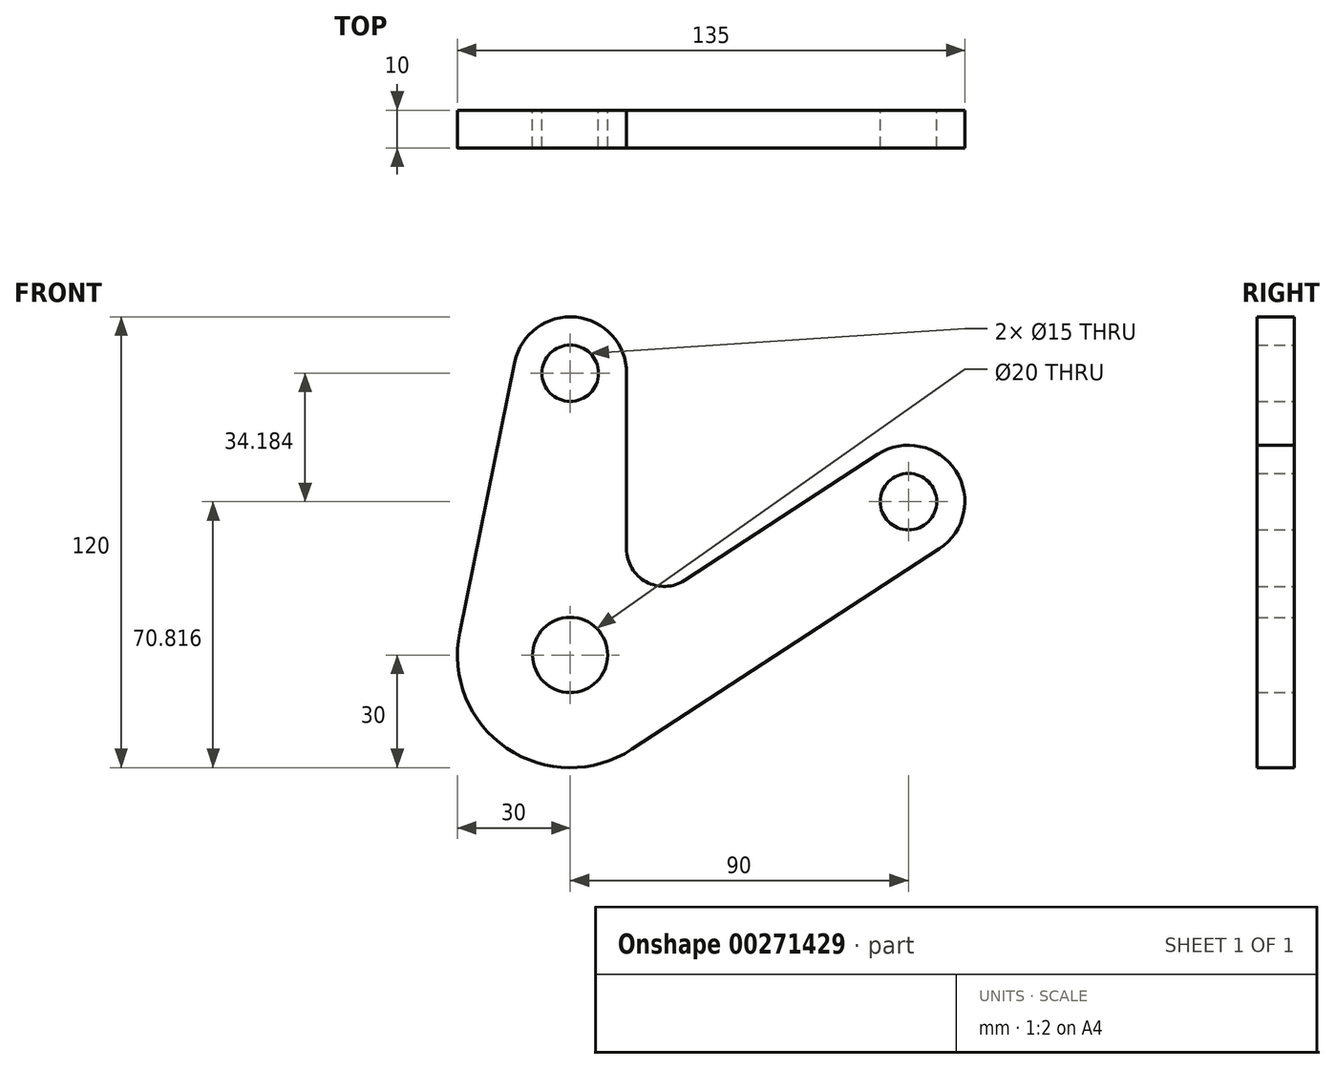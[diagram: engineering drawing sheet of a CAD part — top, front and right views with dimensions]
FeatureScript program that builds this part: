
annotation { "Feature Type Name" : "Feature", "Feature Type Description" : "" }
export const myFeature = defineFeature(function(context is Context, id is Id, definition is map)
    precondition{}
    {
        {
            var Q0;
            Q0=qCreatedBy(makeId("Front.planeOp"),FACE);
            var sketch = newSketch(context, id + "F0", { "sketchPlane" : qUnion([Q0])});
            skCircle(sketch, "E0", {"center": v(0, 0) * mm, "radius": 10 * mm});
            skLineSegment(sketch, "E1", {"start": v(-14.7, 78) * mm, "end": v(-29.4, 6) * mm});
            skArc(sketch, "E2", {"start": v(-29.4, 6) * mm, "mid": v(-16.87, -24.81) * mm, "end": v(16.4, -25.12) * mm});
            skLineSegment(sketch, "E3", {"start": v(15, 75) * mm, "end": v(15, 28.25) * mm});
            skLineSegment(sketch, "E4", {"start": v(30.46, 19.88) * mm, "end": v(81.8, 53.38) * mm});
            skLineSegment(sketch, "E5", {"start": v(16.4, -25.12) * mm, "end": v(98.2, 28.25) * mm});
            skArc(sketch, "E6", {"start": v(-14.7, 78) * mm, "mid": v(1.5, 89.92) * mm, "end": v(15, 75) * mm});
            skArc(sketch, "E7", {"start": v(15, 28.25) * mm, "mid": v(20.24, 19.46) * mm, "end": v(30.46, 19.88) * mm});
            skArc(sketch, "E8", {"start": v(81.8, 53.38) * mm, "mid": v(102.56, 49.01) * mm, "end": v(98.2, 28.25) * mm});
            skCircle(sketch, "E9", {"center": v(0, 75) * mm, "radius": 7.5 * mm});
            skCircle(sketch, "E10", {"center": v(90, 40.82) * mm, "radius": 7.5 * mm});
            skSolve(sketch);
        }
        {
            var Q0;
            Q0 = qSketchRegion(id + "F0", true);
            extrude(context, id + "F1", {"entities" : qUnion([Q0]), "depth" : 10 * mm});
        }
    });
